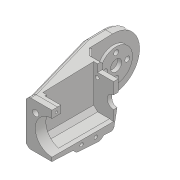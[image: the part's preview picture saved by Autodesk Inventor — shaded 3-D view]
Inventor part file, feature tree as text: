
AUTODESK INVENTOR PART (.ipt)
format: ipt  version: 2018 (Build 220112000, 112)  size: 939,520 bytes
history: native  units: mm
features: sketch x40, extrude x35, projected_geometry x33, hole x10, fillet x10, chamfer x10, mirror x1, plane x1
ambient origin geometry x8: Origin, YZ Plane, XZ Plane, XY Plane, X Axis, Y Axis, Z Axis, Center Point
bodies: Solid1 (feature_tree)
feature tree (140):
  extrude  "Extrusion1"  Depth=45.0mm
  extrude  "Extrusion2"  Depth=2.25mm
  hole  "Hole1"  [1 undecoded]
  hole  "Hole2"  [1 undecoded]
  fillet  "Fillet1"  Radius=14.0mm
  extrude  "Extrusion3"  Depth=18.5mm
  extrude  "Extrusion4"  Depth=10.0mm
  extrude  "Extrusion5"  Depth=2.0mm
  extrude  "Extrusion6"  Depth=2.0mm
  hole  "Hole3"  [1 undecoded]
  extrude  "Extrusion7"  Depth=2.0mm
  extrude  "Extrusion8"  Depth=5.0mm TaperAngle=0.0deg
  extrude  "Extrusion9"  Depth=10.0mm
  extrude  "Extrusion10"  Depth=10.0mm
  extrude  "Extrusion11"  Depth=14.5mm
  extrude  "Extrusion12"  Depth=14.5mm
  extrude  "Extrusion13"  Depth=5.0mm
  extrude  "Extrusion14"  Depth=2.25mm
  extrude  "Extrusion15"  Depth=5.0mm
  extrude  "Extrusion16"  Depth=9.0mm
  extrude  "Extrusion17"  Depth=4.0mm
  chamfer  "Chamfer1"  Distance=1.0mm
  fillet  "Fillet7"  Radius=20.7mm
  fillet  "Fillet8"  Radius=32.0mm
  mirror  "Mirror1"
  extrude  "Extrusion19"  Depth=1.0mm TaperAngle=0.0deg
  extrude  "Extrusion20"  Depth=8.0mm
  extrude  "Extrusion21"  Depth=0.2mm TaperAngle=0.0deg
  extrude  "Extrusion22"  Depth=0.5mm TaperAngle=0.0deg
  sketch  "Sketch29"  dims[d77=12.25mm d78=0.0mm d80=8.0mm]
  extrude  "Extrusion23"  Depth=5.0mm TaperAngle=0.0deg
  extrude  "Extrusion24"  Depth=0.2mm TaperAngle=0.0deg
  plane  "Work Plane1"
  extrude  "Extrusion25"  Depth=2.0mm TaperAngle=45.0deg
  extrude  "Extrusion26"  Depth=0.5mm
  extrude  "Extrusion27"  Depth=4.0mm
  extrude  "Extrusion28"  Depth=3.0mm TaperAngle=0.0deg
  extrude  "Extrusion29"  Depth=33.0mm
  extrude  "Extrusion30"  Depth=56.0mm
  extrude  "Extrusion31"  Depth=25.0mm TaperAngle=0.0deg
  chamfer  "Chamfer2"  Distance=6.0mm
  hole  "Hole6"  [1 undecoded]
  chamfer  "Chamfer3"  Distance=40.0mm
  extrude  "Extrusion32"  Depth=28.25mm
  extrude  "Extrusion33"  Depth=28.25mm
  chamfer  "Chamfer4"  Distance=12.0mm
  chamfer  "Chamfer5"  Distance=40.0mm
  chamfer  "Chamfer6"  Distance=40.0mm
  fillet  "Fillet9"  Radius=20.5mm
  extrude  "Extrusion34"  Depth=28.25mm TaperAngle=0.0deg
  chamfer  "Chamfer7"  Distance=20.5mm
  sketch  "Sketch42"  dims[d146=6.0mm d147=0.0mm d149=42.0mm]
  hole  "Hole7"  [1 undecoded]
  hole  "Hole8"  [1 undecoded]
  hole  "Hole9"  [1 undecoded]
  fillet  "Fillet10"  Radius=2.0mm
  chamfer  "Chamfer8"  Distance=7.0mm
  chamfer  "Chamfer9"  Distance=2.5mm
  fillet  "Fillet11"  Radius=7.0mm
  fillet  "Fillet12"  Radius=2.5mm
  extrude  "Extrusion35"  Depth=3.0mm TaperAngle=45.0deg
  sketch  "Sketch45"  dims[d151=4.5mm]
  hole  "Hole10"  [1 undecoded]
  hole  "Hole11"  [1 undecoded]
  hole  "Hole12"  [1 undecoded]
  fillet  "Fillet13"  Radius=12.0mm
  fillet  "Fillet14"  Radius=2.0mm
  fillet  "Fillet15"  Radius=15.0mm
  chamfer  "Chamfer10"  Distance=20.0mm
  extrude  "Extrusion36"  Depth=2.0mm TaperAngle=45.0deg
  sketch  "Sketch1"  dims[d0=24.5mm d1=45.0mm]
  sketch  "Sketch2"  dims[d2=1.95mm d3=0.0mm d4=2.25mm]
  projected_geometry  "Projected Loop1"
  sketch  "Sketch3"  dims[d5=20.0mm d6=2.25mm]
  projected_geometry  "Projected Loop2"
  sketch  "Sketch4"  dims[d7=5.25mm d8=5.25mm d9=14.0mm]
  projected_geometry  "Projected Loop3"
  sketch  "Sketch5"  dims[d10=5.25mm d11=18.5mm]
  projected_geometry  "Projected Loop4"
  sketch  "Sketch6"  dims[d12=10.0mm d13=0.0mm d14=20.5mm]
  projected_geometry  "Projected Loop5"
  sketch  "Sketch7"  dims[d15=2.0mm d16=2.195mm]
  projected_geometry  "Projected Loop6"
  sketch  "Sketch8"  dims[d17=2.0mm]
  projected_geometry  "Projected Loop7"
  sketch  "Sketch9"  dims[d18=2.4mm d19=6.0mm d20=4.4mm d21=2.0mm d22=90.0deg d23=8.0mm d24=20.594885mm d25=20.5mm]
  projected_geometry  "Projected Loop8"
  projected_geometry  "Projected Loop9"
  sketch  "Sketch10"  dims[d26=26.65mm d27=2.0mm]
  projected_geometry  "Projected Loop10"
  projected_geometry  "Projected Loop11"
  sketch  "Sketch11"  dims[d28=2.0mm]
  projected_geometry  "Projected Loop12"
  sketch  "Sketch12"  dims[d29=2.4mm d30=6.0mm d31=4.4mm d32=2.0mm d33=90.0deg d34=8.0mm d35=20.594885mm d36=0.5mm]
  sketch  "Sketch13"  dims[d37=18.0mm d38=5.0mm d39=0.0mm]
  sketch  "Sketch14"  dims[d41=10.0mm d42=0.0mm d43=24.5mm]
  projected_geometry  "Projected Loop13"
  sketch  "Sketch15"  dims[d44=1.15mm d45=0.0mm d46=10.0mm]
  sketch  "Sketch16"  dims[d47=21.0mm d48=14.5mm]
  projected_geometry  "Projected Loop14"
  sketch  "Sketch17"  dims[d49=20.0mm d50=14.5mm]
  projected_geometry  "Projected Loop15"
  sketch  "Sketch18"  dims[d51=24.5mm d52=5.0mm]
  projected_geometry  "Projected Loop16"
  sketch  "Sketch19"  dims[d53=5.0mm d54=2.25mm]
  projected_geometry  "Projected Loop17"
  sketch  "Sketch20"  dims[d55=2.25mm d56=5.0mm]
  projected_geometry  "Projected Loop18"
  sketch  "Sketch25"  dims[d57=5.0mm d58=9.0mm]
  projected_geometry  "Projected Loop22"
  sketch  "Sketch26"  dims[d59=14.75mm d60=4.0mm d61=1.0mm d62=0.0mm d63=20.7mm]
  sketch  "Sketch27"  dims[d64=2.4mm d65=6.0mm d66=4.4mm d67=2.0mm d68=90.0deg d69=8.0mm d70=20.594885mm d72=32.0mm]
  projected_geometry  "Projected Loop23"
  sketch  "Sketch28"  dims[d73=5.0mm d74=0.0mm d75=1.0mm d76=0.0mm]
  projected_geometry  "Projected Loop24"
  sketch  "Sketch31"  dims[d81=4.5mm d82=0.0mm d84=0.2mm d85=0.0mm]
  projected_geometry  "Projected Loop25"
  sketch  "Sketch32"  dims[d86=21.0mm d87=0.5mm d88=0.0mm]
  projected_geometry  "Projected Loop26"
  sketch  "Sketch33"  dims[d91=8.0mm d92=0.0mm d93=5.0mm d94=0.0mm]
  sketch  "Sketch34"  dims[d95=5.0mm d96=0.0mm d98=0.2mm d99=0.0mm]
  sketch  "Sketch35"  dims[d100=0.2mm d101=0.0mm d102=2.5mm d103=2.0mm d104=45.0deg]
  projected_geometry  "Projected Loop27"
  sketch  "Sketch36"  dims[d105=1.5mm d114=0.5mm]
  sketch  "Sketch37"  dims[d128=4.0mm d129=0.0mm d130=8.0mm]
  sketch  "Sketch38"  dims[d131=3.0mm d132=0.0mm d133=3.0mm d134=0.0mm]
  projected_geometry  "Projected Loop28"
  sketch  "Sketch39"  dims[d135=25.0mm d136=0.0mm d137=33.0mm]
  projected_geometry  "Projected Loop29"
  sketch  "Sketch40"  dims[d138=2.5mm d139=56.0mm]
  projected_geometry  "Projected Loop30"
  sketch  "Sketch41"  dims[d140=25.0mm d141=0.0mm d142=25.0mm d143=0.0mm d144=6.0mm d145=0.0mm]
  sketch  "Sketch44"  dims[d150=4.5mm]
  projected_geometry  "Projected Loop31"
  projected_geometry  "Projected Loop32"
  projected_geometry  "Projected Loop33"
  sketch  "Sketch46"  dims[d152=4.5mm d153=40.0mm d154=0.0mm d155=28.0mm d156=12.0mm d157=12.0mm d158=40.0mm d159=0.0mm d160=40.0mm d161=0.0mm d162=20.5mm d163=1.8mm d164=0.0mm d165=20.5mm d166=3.3mm d167=0.0mm d168=2.0mm d169=2.0mm d170=45.0deg d171=14.0mm d172=3.1mm d173=6.0mm d174=6.3mm d175=2.0mm d176=90.0deg d177=8.0mm d178=20.594885mm d179=1.2mm d180=2.0mm d181=45.0deg d182=7.0mm d183=2.5mm d184=0.0mm d185=7.0mm d186=2.5mm d187=0.0mm d188=3.0mm d189=15.0mm d190=45.0deg d191=3.0mm d192=15.0mm d193=45.0deg d194=3.0mm d195=15.0mm d196=45.0deg d197=2.0mm d198=12.0mm d199=2.0mm d200=15.0mm d201=20.0mm d202=0.0mm d203=2.0mm d204=15.0mm d205=45.0deg d206=2.9mm d207=2.9mm d208=3.18mm d209=3.18mm d210=4.0mm d211=6.0mm d212=6.3mm d213=2.0mm d214=90.0deg d215=8.0mm d216=20.594885mm d217=1.567mm d218=25.0mm d219=6.3mm d220=2.0mm d221=90.0deg d222=25.0mm d223=20.594885mm d224=2.15mm d225=20.0mm d226=4.4mm d227=2.0mm d228=90.0deg d229=10.0mm d230=0.0mm d231=0.5mm d232=2.0mm d233=15.0mm d234=45.0deg d235=2.0mm d236=15.0mm d237=45.0deg d238=1.0mm d239=3.0mm d240=3.9mm d241=3.9mm d242=3.5mm d243=0.0mm d244=2.75mm d245=2.75mm d246=2.5mm d247=1.567mm d248=4.0mm d249=4.4mm d250=2.0mm d251=90.0deg d252=40.0mm d253=20.594885mm d254=2.1mm d255=4.0mm d256=4.4mm d257=2.0mm d258=90.0deg d259=28.25mm d260=0.0mm d261=3.9mm d262=4.0mm d263=4.4mm d264=2.0mm d265=90.0deg d266=20.0mm d267=0.0mm d268=0.2mm d269=2.0mm d270=2.0mm d271=1.8mm d272=15.0mm d273=45.0deg d274=28.25mm d275=0.0mm]
  projected_geometry  "Project Cut Edges1"
  projected_geometry  "Project Cut Edges2"
  projected_geometry  "Project Cut Edges3"
note: 10 required parameter values undecoded (feature->parameter linkage not recoverable at this tier; creation-order binding heuristic only, values carry confidence <= 0.55)
